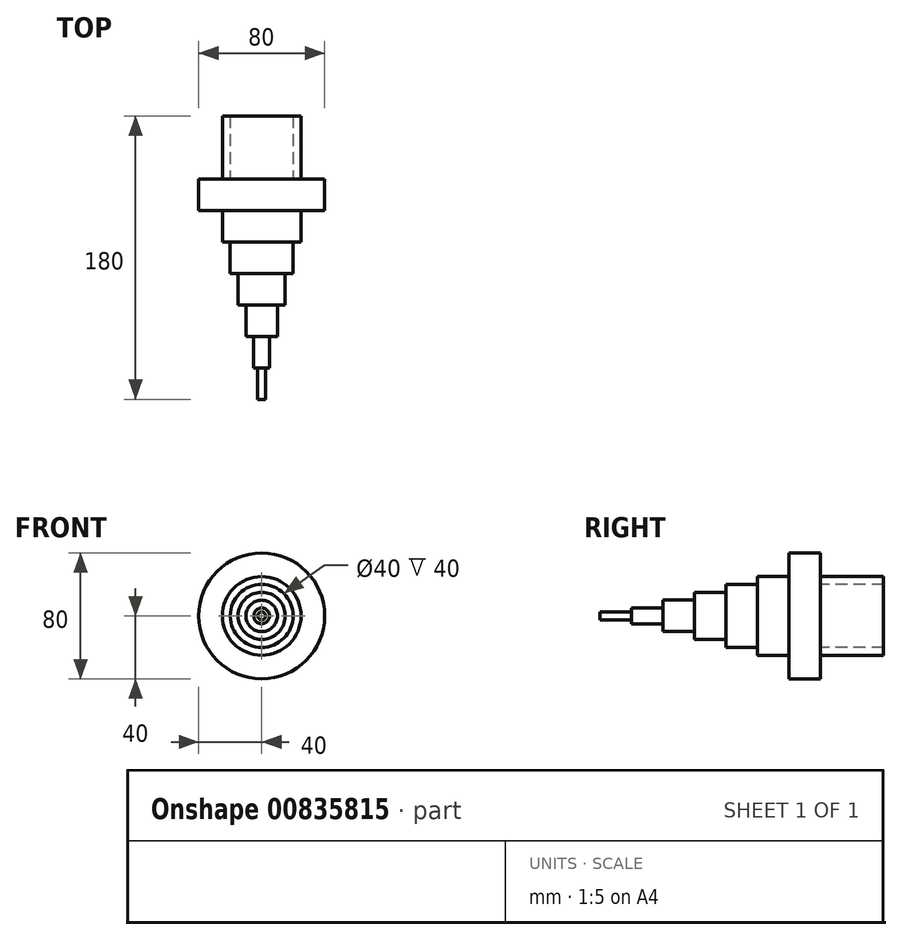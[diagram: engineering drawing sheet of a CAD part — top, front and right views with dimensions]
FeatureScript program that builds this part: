
annotation { "Feature Type Name" : "Feature", "Feature Type Description" : "" }
export const myFeature = defineFeature(function(context is Context, id is Id, definition is map)
    precondition{}
    {
        {
            var Q0;
            Q0=qCreatedBy(makeId("Front.planeOp"),FACE);
            var sketch = newSketch(context, id + "F0", { "sketchPlane" : qUnion([Q0])});
            skCircle(sketch, "E0", {"center": v(0, 0) * mm, "radius": 2.5 * mm});
            skCircle(sketch, "E1", {"center": v(0, 0) * mm, "radius": 5 * mm});
            skCircle(sketch, "E2", {"center": v(0, 0) * mm, "radius": 10 * mm});
            skCircle(sketch, "E3", {"center": v(0, 0) * mm, "radius": 15 * mm});
            skCircle(sketch, "E4", {"center": v(0, 0) * mm, "radius": 20 * mm});
            skCircle(sketch, "E5", {"center": v(0, 0) * mm, "radius": 25 * mm});
            skCircle(sketch, "E6", {"center": v(0, 0) * mm, "radius": 40 * mm});
            skSolve(sketch);
        }
        {
            var Q0;
            Q0=makeQuery(id+"F0.imprint","IMPRINT",FACE,{"disambiguationData":[TD([[makeQuery(id+"F0.imprint","IMPRINT",EDGE,{"derivedFrom":sQuery(id+"F0.wireOp",EDGE,"E0")}),1.0]])]});
            extrude(context, id + "F1", {"entities" : qUnion([Q0]), "depth" : 140 * mm, "offsetDistance" : 25 * mm});
        }
        {
            var Q0;
            Q0=makeQuery(id+"F0.imprint","IMPRINT",FACE,{"disambiguationData":[TD([[makeQuery(id+"F0.imprint","IMPRINT",EDGE,{"derivedFrom":sQuery(id+"F0.wireOp",EDGE,"E0")}),-1.0]])]});
            extrude(context, id + "F2", {"entities" : qUnion([Q0]), "operationType" : NewBodyOperationType.ADD, "depth" : 120 * mm, "offsetDistance" : 25 * mm});
        }
        {
            var Q0;
            Q0=makeQuery(id+"F0.imprint","IMPRINT",FACE,{"disambiguationData":[TD([[makeQuery(id+"F0.imprint","IMPRINT",EDGE,{"derivedFrom":sQuery(id+"F0.wireOp",EDGE,"E1")}),-1.0]])]});
            extrude(context, id + "F3", {"entities" : qUnion([Q0]), "operationType" : NewBodyOperationType.ADD, "depth" : 100 * mm, "offsetDistance" : 25 * mm});
        }
        {
            var Q0;
            Q0=makeQuery(id+"F0.imprint","IMPRINT",FACE,{"disambiguationData":[TD([[makeQuery(id+"F0.imprint","IMPRINT",EDGE,{"derivedFrom":sQuery(id+"F0.wireOp",EDGE,"E2")}),-1.0]])]});
            extrude(context, id + "F4", {"entities" : qUnion([Q0]), "operationType" : NewBodyOperationType.ADD, "depth" : 80 * mm, "offsetDistance" : 25 * mm});
        }
        {
            var Q0;
            Q0=makeQuery(id+"F0.imprint","IMPRINT",FACE,{"disambiguationData":[TD([[makeQuery(id+"F0.imprint","IMPRINT",EDGE,{"derivedFrom":sQuery(id+"F0.wireOp",EDGE,"E3")}),-1.0]])]});
            extrude(context, id + "F5", {"entities" : qUnion([Q0]), "operationType" : NewBodyOperationType.ADD, "depth" : 60 * mm, "offsetDistance" : 25 * mm});
        }
        {
            var Q0;
            Q0=makeQuery(id+"F0.imprint","IMPRINT",FACE,{"disambiguationData":[TD([[makeQuery(id+"F0.imprint","IMPRINT",EDGE,{"derivedFrom":sQuery(id+"F0.wireOp",EDGE,"E4")}),-1.0]])]});
            extrude(context, id + "F6", {"entities" : qUnion([Q0]), "operationType" : NewBodyOperationType.ADD, "depth" : 40 * mm, "offsetDistance" : 25 * mm});
        }
        {
            var Q0;
            Q0=makeQuery(id+"F0.imprint","IMPRINT",FACE,{"disambiguationData":[TD([[makeQuery(id+"F0.imprint","IMPRINT",EDGE,{"derivedFrom":sQuery(id+"F0.wireOp",EDGE,"E5")}),-1.0]])]});
            extrude(context, id + "F7", {"entities" : qUnion([Q0]), "operationType" : NewBodyOperationType.ADD, "depth" : 20 * mm, "offsetDistance" : 25 * mm});
        }
        {
            var Q0;
            Q0=makeQuery(id+"F0.imprint","IMPRINT",FACE,{"disambiguationData":[TD([[makeQuery(id+"F0.imprint","IMPRINT",EDGE,{"derivedFrom":sQuery(id+"F0.wireOp",EDGE,"E4")}),-1.0]])]});
            extrude(context, id + "F8", {"entities" : qUnion([Q0]), "operationType" : NewBodyOperationType.ADD, "oppositeDirection" : true, "depth" : 40 * mm, "offsetDistance" : 25 * mm});
        }
    });
